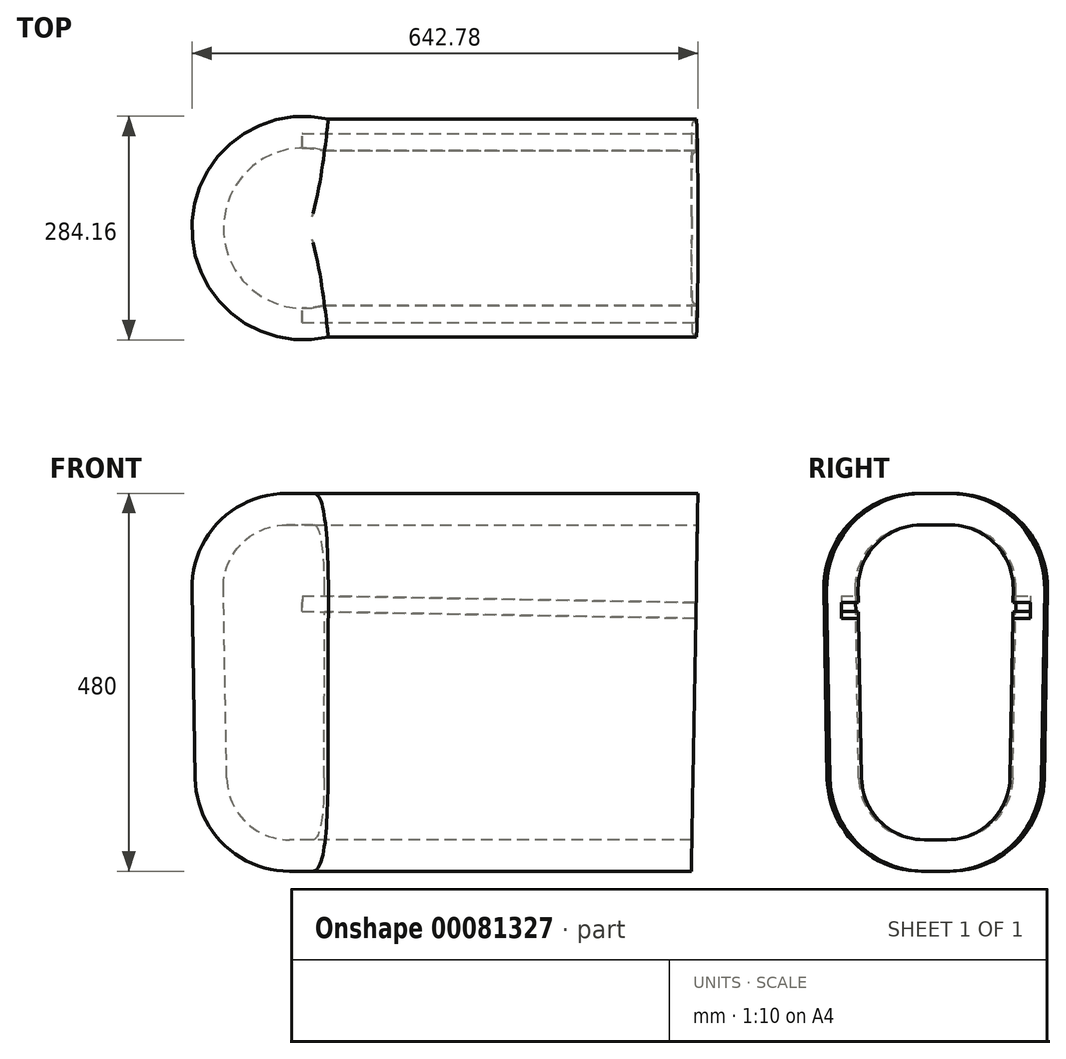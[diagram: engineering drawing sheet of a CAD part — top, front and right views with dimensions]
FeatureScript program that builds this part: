
annotation { "Feature Type Name" : "Feature", "Feature Type Description" : "" }
export const myFeature = defineFeature(function(context is Context, id is Id, definition is map)
    precondition{}
    {
        {
            var Q0;
            Q0=qCreatedBy(makeId("Top.planeOp"),FACE);
            var sketch = newSketch(context, id + "F0", { "sketchPlane" : qUnion([Q0])});
            skCircle(sketch, "E0", {"center": v(0, 0) * mm, "radius": 100 * mm});
            skSolve(sketch);
        }
        {
            var Q0;
            Q0 = qSketchRegion(id + "F0", true);
            extrude(context, id + "F1", {"entities" : qUnion([Q0]), "depth" : 200 * mm, "hasDraft" : true, "draftAngle" : 1 * degree, "hasSecondDirection" : true, "secondDirectionOppositeDirection" : true, "secondDirectionDepth" : 200 * mm, "hasSecondDirectionDraft" : true, "secondDirectionDraftAngle" : 1 * degree, "secondDirectionDraftPullDirection" : true});
        }
        {
            var Q0;
            Q0=makeQuery(id+"F1.opExtrude","CAP_FACE",FACE,{"disambiguationData":[OSD([sQuery(id+"F0.wireOp",EDGE,"E0")])],"isStart":false});
            var sketch = newSketch(context, id + "F2", { "sketchPlane" : qUnion([Q0])});
            skLineSegment(sketch, "E1.bottom", {"start": v(0, 100) * mm, "end": v(500, 100) * mm});
            skLineSegment(sketch, "E1.top", {"start": v(0, -100) * mm, "end": v(500, -100) * mm});
            skLineSegment(sketch, "E1.left", {"start": v(0, 100) * mm, "end": v(0, -100) * mm});
            skLineSegment(sketch, "E1.right", {"start": v(500, 100) * mm, "end": v(500, -100) * mm});
            skSolve(sketch);
        }
        {
            var Q0;
            Q0 = qSketchRegion(id + "F2", true);
            var Q1;
            Q1=makeQuery(id+"F1.opExtrude","CAP_FACE",FACE,{"disambiguationData":[OSD([sQuery(id+"F0.wireOp",EDGE,"E0")])],"isStart":true});
            extrude(context, id + "F3", {"entities" : qUnion([Q0]), "operationType" : NewBodyOperationType.ADD, "endBound" : BoundingType.UP_TO_SURFACE, "oppositeDirection" : true, "endBoundEntityFace" : qUnion([Q1]), "depth" : 25 * mm, "hasDraft" : true, "draftAngle" : 1 * degree, "draftPullDirection" : true});
        }
        {
            var Q0;
            Q0=makeQuery(id+"F3.opExtrude","CAP_EDGE",EDGE,{"disambiguationData":[OSD([sQuery(id+"F2.wireOp",EDGE,"E1.top")])],"isStart":true});
            var Q1;
            Q1=makeQuery(id+"F1.opExtrude","CAP_EDGE",EDGE,{"disambiguationData":[OSD([sQuery(id+"F0.wireOp",EDGE,"E0")])],"isStart":false});
            var Q2;
            Q2=makeQuery(id+"F3.opExtrude","CAP_EDGE",EDGE,{"disambiguationData":[OSD([sQuery(id+"F2.wireOp",EDGE,"E1.bottom")])],"isStart":true});
            var Q3;
            Q3=makeQuery(id+"F3.opExtrude","CAP_EDGE",EDGE,{"disambiguationData":[OSD([sQuery(id+"F2.wireOp",EDGE,"E1.top")])],"isStart":false});
            var Q4;
            Q4=makeQuery(id+"F1.opExtrude","CAP_EDGE",EDGE,{"disambiguationData":[OSD([sQuery(id+"F0.wireOp",EDGE,"E0")])],"isStart":true});
            var Q5;
            Q5=makeQuery(id+"F3.opExtrude","CAP_EDGE",EDGE,{"disambiguationData":[OSD([sQuery(id+"F2.wireOp",EDGE,"E1.bottom")])],"isStart":false});
            fillet(context, id + "F4", {"entities" : qUnion([Q0, Q1, Q2, Q3, Q4, Q5]), "radius" : 80 * mm, "tangentPropagation" : true, "allowEdgeOverflow" : false});
        }
        {
            var Q0;
            Q0=makeQuery(id+"F3.opExtrude","SWEPT_FACE",FACE,{"disambiguationData":[OSD([sQuery(id+"F2.wireOp",EDGE,"E1.right")])]});
            shell(context, id + "F5", {"entities" : qUnion([Q0]), "thickness" : 40 * mm, "oppositeDirection" : true});
        }
        {
            var Q0;
            Q0=makeQuery(id+"F3.opExtrude","SWEPT_FACE",FACE,{"disambiguationData":[OSD([sQuery(id+"F2.wireOp",EDGE,"E1.right")])]});
            var sketch = newSketch(context, id + "F6", { "sketchPlane" : qUnion([Q0])});
            skLineSegment(sketch, "E2.bottom", {"start": v(-120, 110) * mm, "end": v(120, 110) * mm});
            skLineSegment(sketch, "E2.top", {"start": v(-120, 90) * mm, "end": v(120, 90) * mm});
            skLineSegment(sketch, "E2.left", {"start": v(-120, 110) * mm, "end": v(-120, 90) * mm});
            skLineSegment(sketch, "E2.right", {"start": v(120, 110) * mm, "end": v(120, 90) * mm});
            skLineSegment(sketch, "E3", {"start": v(0, 90) * mm, "end": v(0, 0) * mm, "construction": true});
            skSolve(sketch);
        }
        {
            var Q0;
            Q0 = qSketchRegion(id + "F6", true);
            extrude(context, id + "F7", {"entities" : qUnion([Q0]), "operationType" : NewBodyOperationType.REMOVE, "oppositeDirection" : true, "depth" : 500 * mm});
        }
    });
